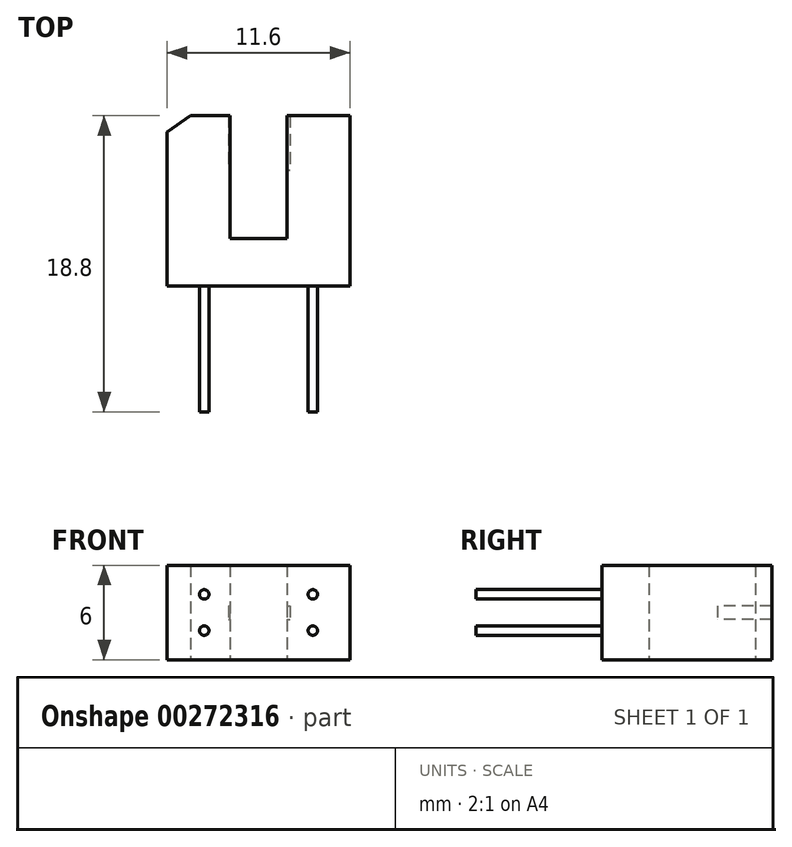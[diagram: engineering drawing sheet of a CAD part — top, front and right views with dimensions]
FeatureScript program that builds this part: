
annotation { "Feature Type Name" : "Feature", "Feature Type Description" : "" }
export const myFeature = defineFeature(function(context is Context, id is Id, definition is map)
    precondition{}
    {
        {
            var Q0;
            Q0=qCreatedBy(makeId("Top.planeOp"),FACE);
            var sketch = newSketch(context, id + "F0", { "sketchPlane" : qUnion([Q0])});
            skLineSegment(sketch, "E0", {"start": v(-98.64, -79.54) * mm, "end": v(-87.04, -79.54) * mm});
            skLineSegment(sketch, "E1", {"start": v(-87.04, -79.54) * mm, "end": v(-87.04, -68.74) * mm});
            skLineSegment(sketch, "E2", {"start": v(-87.04, -68.74) * mm, "end": v(-91.04, -68.74) * mm});
            skLineSegment(sketch, "E3", {"start": v(-91.04, -68.74) * mm, "end": v(-91.04, -76.54) * mm});
            skLineSegment(sketch, "E4", {"start": v(-91.04, -76.54) * mm, "end": v(-94.64, -76.54) * mm});
            skLineSegment(sketch, "E5", {"start": v(-94.64, -76.54) * mm, "end": v(-94.64, -68.74) * mm});
            skLineSegment(sketch, "E6", {"start": v(-94.64, -68.74) * mm, "end": v(-97.14, -68.74) * mm});
            skLineSegment(sketch, "E7", {"start": v(-97.14, -68.74) * mm, "end": v(-98.64, -69.78) * mm});
            skLineSegment(sketch, "E8", {"start": v(-98.64, -69.78) * mm, "end": v(-98.64, -79.54) * mm});
            skPoint(sketch, "E9", {"position": v(-92.84, -70.47) * mm});
            skLineSegment(sketch, "E10", {"start": v(-94.64, -70.47) * mm, "end": v(-91.04, -70.47) * mm, "construction": true});
            skSolve(sketch);
        }
        {
            var Q0;
            Q0=makeQuery(id+"F0.imprint","IMPRINT",FACE,{"disambiguationData":[TD([[makeQuery(id+"F0.imprint","IMPRINT",EDGE,{"derivedFrom":sQuery(id+"F0.wireOp",EDGE,"E0")}),1.0]])]});
            extrude(context, id + "F1", {"entities" : qUnion([Q0]), "depth" : 6 * mm});
        }
        {
            var Q0;
            Q0=makeQuery(id+"F1.opExtrude","SWEPT_FACE",FACE,{"disambiguationData":[OSD([sQuery(id+"F0.wireOp",EDGE,"E5")])]});
            var sketch = newSketch(context, id + "F2", { "sketchPlane" : qUnion([Q0])});
            skLineSegment(sketch, "E11.bottom", {"start": v(-68.74, 3.42) * mm, "end": v(-72.2, 3.42) * mm});
            skLineSegment(sketch, "E11.top", {"start": v(-68.74, 2.57) * mm, "end": v(-72.2, 2.57) * mm});
            skLineSegment(sketch, "E11.left", {"start": v(-68.74, 3.42) * mm, "end": v(-68.74, 2.57) * mm});
            skLineSegment(sketch, "E11.right", {"start": v(-72.2, 3.42) * mm, "end": v(-72.2, 2.57) * mm});
            skSolve(sketch);
        }
        {
            var Q0;
            Q0=makeQuery(id+"F2.imprint","IMPRINT",FACE,{"disambiguationData":[TD([[makeQuery(id+"F2.imprint","IMPRINT",EDGE,{"derivedFrom":sQuery(id+"F2.wireOp",EDGE,"E11.bottom")}),1.0]])]});
            extrude(context, id + "F3", {"entities" : qUnion([Q0]), "operationType" : NewBodyOperationType.REMOVE, "oppositeDirection" : true, "depth" : 0.1 * mm, "hasSecondDirection" : true, "secondDirectionOppositeDirection" : false, "secondDirectionDepth" : 3.8 * mm});
        }
        {
            var Q0;
            Q0=makeQuery(id+"F1.opExtrude","SWEPT_FACE",FACE,{"disambiguationData":[OSD([sQuery(id+"F0.wireOp",EDGE,"E0")])]});
            var sketch = newSketch(context, id + "F4", { "sketchPlane" : qUnion([Q0])});
            skCircle(sketch, "E12", {"center": v(-96.3, 4.15) * mm, "radius": 0.3 * mm});
            skCircle(sketch, "E13", {"center": v(-96.3, 1.85) * mm, "radius": 0.3 * mm});
            skCircle(sketch, "E14", {"center": v(-89.4, 4.15) * mm, "radius": 0.3 * mm});
            skCircle(sketch, "E15", {"center": v(-89.4, 1.85) * mm, "radius": 0.3 * mm});
            skLineSegment(sketch, "E16", {"start": v(-96.3, 4.15) * mm, "end": v(-96.3, 1.85) * mm, "construction": true});
            skLineSegment(sketch, "E17", {"start": v(-89.4, 4.15) * mm, "end": v(-89.4, 1.85) * mm, "construction": true});
            skLineSegment(sketch, "E18", {"start": v(-96.3, 3) * mm, "end": v(-89.4, 3) * mm, "construction": true});
            skLineSegment(sketch, "E19", {"start": v(-92.84, 6) * mm, "end": v(-92.84, 0) * mm, "construction": true});
            skPoint(sketch, "E20", {"position": v(-92.84, 3) * mm});
            skSolve(sketch);
        }
        {
            var Q0;
            Q0 = qSketchRegion(id + "F4", true);
            extrude(context, id + "F5", {"entities" : qUnion([Q0]), "operationType" : NewBodyOperationType.ADD, "depth" : 8 * mm});
        }
    });
